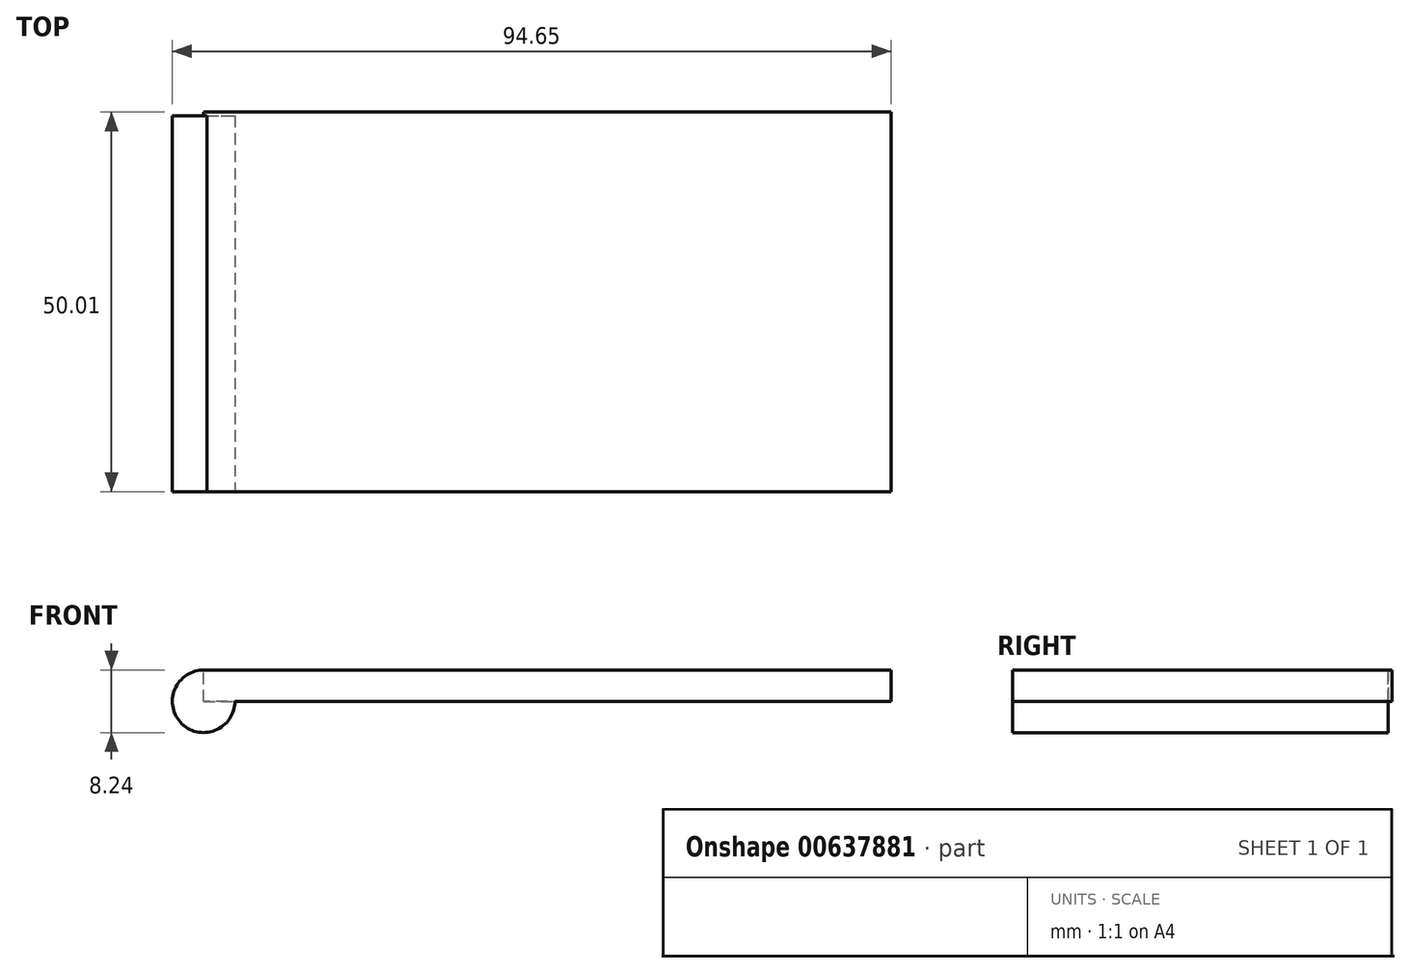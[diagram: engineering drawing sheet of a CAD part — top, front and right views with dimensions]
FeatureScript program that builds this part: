
annotation { "Feature Type Name" : "Feature", "Feature Type Description" : "" }
export const myFeature = defineFeature(function(context is Context, id is Id, definition is map)
    precondition{}
    {
        {
            var Q0;
            Q0=qCreatedBy(makeId("Top.planeOp"),FACE);
            var sketch = newSketch(context, id + "F0", { "sketchPlane" : qUnion([Q0])});
            skLineSegment(sketch, "E0.bottom", {"start": v(43.54, -39.8) * mm, "end": v(-47, -39.8) * mm});
            skLineSegment(sketch, "E0.top", {"start": v(43.54, 10.2) * mm, "end": v(-47, 10.2) * mm});
            skLineSegment(sketch, "E0.left", {"start": v(43.54, -39.8) * mm, "end": v(43.54, 10.2) * mm});
            skLineSegment(sketch, "E0.right", {"start": v(-47, -39.8) * mm, "end": v(-47, 10.2) * mm});
            skSolve(sketch);
        }
        {
            var Q0;
            Q0 = qSketchRegion(id + "F0", true);
            extrude(context, id + "F1", {"entities" : qUnion([Q0]), "depth" : 4.1 * mm, "offsetDistance" : 25 * mm});
        }
        {
            var Q0;
            Q0=makeQuery(id+"F1.opExtrude","SWEPT_FACE",FACE,{"disambiguationData":[OSD([sQuery(id+"F0.wireOp",EDGE,"E0.bottom")])]});
            var sketch = newSketch(context, id + "F2", { "sketchPlane" : qUnion([Q0])});
            skCircle(sketch, "E1", {"center": v(-47, 0) * mm, "radius": 4.12 * mm});
            skSolve(sketch);
        }
        {
            var Q0;
            Q0 = qSketchRegion(id + "F2", true);
            extrude(context, id + "F3", {"entities" : qUnion([Q0]), "operationType" : NewBodyOperationType.ADD, "oppositeDirection" : true, "depth" : 49.5 * mm, "offsetDistance" : 25 * mm});
        }
    });
